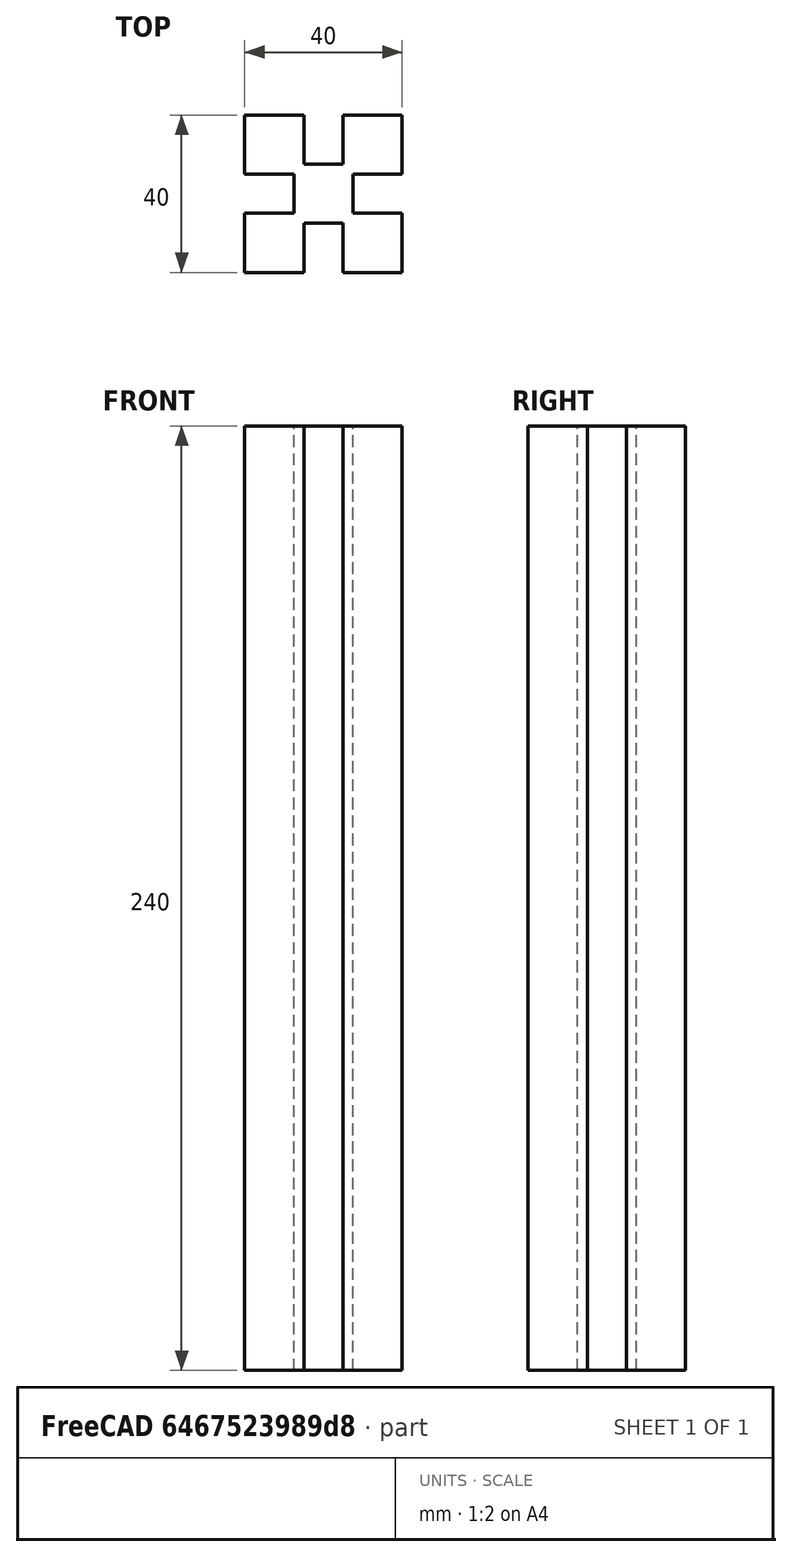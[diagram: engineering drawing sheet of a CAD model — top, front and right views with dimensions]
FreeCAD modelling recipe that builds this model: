
FCSTD DOCUMENT  (FreeCAD 0.18R14555 (Git shallow))
Label: t-slot-profile-240
License: All rights reserved
LicenseURL: http://en.wikipedia.org/wiki/All_rights_reserved
objects: Sketcher::SketchObject×1, PartDesign::Pad×1, PartDesign::Body×1
note: 4 computed .brp shape members not serialized (recipe doc carries the construction recipe); baked Part::Feature solids carry a one-line shape summary decoded from their .brp

FEATURE [Sketcher::SketchObject] Sketch
  MapMode = 5
  Support = -> [XY_Plane]
  sketch-geometry (30):
    g0: LineSegment StartX=-20 StartY=-20 StartZ=0 EndX=-20 EndY=-5 EndZ=0
    g1: LineSegment StartX=-20 StartY=-5 StartZ=0 EndX=-7.5 EndY=-5 EndZ=0
    g2: LineSegment StartX=-7.5 StartY=-5 StartZ=0 EndX=-7.5 EndY=5 EndZ=0
    g3: LineSegment StartX=-7.5 StartY=5 StartZ=0 EndX=-20 EndY=5 EndZ=0
    g4: LineSegment StartX=-20 StartY=5 StartZ=0 EndX=-20 EndY=20 EndZ=0
    g5: LineSegment StartX=-20 StartY=20 StartZ=0 EndX=-5 EndY=20 EndZ=0
    g6: LineSegment StartX=-5 StartY=20 StartZ=0 EndX=-5 EndY=7.5 EndZ=0
    g7: LineSegment StartX=-5 StartY=7.5 StartZ=0 EndX=5 EndY=7.5 EndZ=0
    g8: LineSegment StartX=5 StartY=7.5 StartZ=0 EndX=5 EndY=20 EndZ=0
    g9: LineSegment StartX=5 StartY=20 StartZ=0 EndX=20 EndY=20 EndZ=0
    g10: LineSegment StartX=20 StartY=20 StartZ=0 EndX=20 EndY=5 EndZ=0
    g11: LineSegment StartX=20 StartY=5 StartZ=0 EndX=7.5 EndY=5 EndZ=0
    g12: LineSegment StartX=7.5 StartY=5 StartZ=0 EndX=7.5 EndY=-5 EndZ=0
    g13: LineSegment StartX=7.5 StartY=-5 StartZ=0 EndX=20 EndY=-5 EndZ=0
    g14: LineSegment StartX=20 StartY=-5 StartZ=0 EndX=20 EndY=-20 EndZ=0
    g15: LineSegment StartX=20 StartY=-20 StartZ=0 EndX=5 EndY=-20 EndZ=0
    g16: LineSegment StartX=5 StartY=-20 StartZ=0 EndX=5 EndY=-7.5 EndZ=0
    g17: LineSegment StartX=5 StartY=-7.5 StartZ=0 EndX=-5 EndY=-7.5 EndZ=0
    g18: LineSegment StartX=-5 StartY=-7.5 StartZ=0 EndX=-5 EndY=-20 EndZ=0
    g19: LineSegment StartX=-5 StartY=-20 StartZ=0 EndX=-20 EndY=-20 EndZ=0
    g20: LineSegment [constr] StartX=-5 StartY=-7.5 StartZ=0 EndX=-5 EndY=7.5 EndZ=0
    g21: LineSegment [constr] StartX=5 StartY=7.5 StartZ=0 EndX=5 EndY=-7.5 EndZ=0
    g22: LineSegment [constr] StartX=-7.5 StartY=5 StartZ=0 EndX=7.5 EndY=5 EndZ=0
    g23: LineSegment [constr] StartX=7.5 StartY=-5 StartZ=0 EndX=-7.5 EndY=-5 EndZ=0
    g24: LineSegment [constr] StartX=-20 StartY=-5 StartZ=0 EndX=-20 EndY=5 EndZ=0
    g25: LineSegment [constr] StartX=-5 StartY=20 StartZ=0 EndX=5 EndY=20 EndZ=0
    g26: LineSegment [constr] StartX=20 StartY=5 StartZ=0 EndX=20 EndY=-5 EndZ=0
    g27: LineSegment [constr] StartX=-5 StartY=-20 StartZ=0 EndX=5 EndY=-20 EndZ=0
    g28: LineSegment [constr] StartX=20 StartY=-20 StartZ=0 EndX=-20 EndY=20 EndZ=0
    g29: LineSegment [constr] StartX=-20 StartY=-20 StartZ=0 EndX=20 EndY=20 EndZ=0
  constraints (80):
    c: Vertical(g0)
    c: Coincident(g0,g1)
    c: Horizontal(g1)
    c: Coincident(g1,g2)
    c: Vertical(g2)
    c: Coincident(g2,g3)
    c: Horizontal(g3)
    c: Coincident(g3,g4)
    c: Vertical(g4)
    c: Coincident(g4,g5)
    c: Horizontal(g5)
    c: Coincident(g5,g6)
    c: Vertical(g6)
    c: Coincident(g6,g7)
    c: Horizontal(g7)
    c: Coincident(g7,g8)
    c: Vertical(g8)
    c: Coincident(g8,g9)
    c: Horizontal(g9)
    c: Coincident(g9,g10)
    c: Vertical(g10)
    c: Coincident(g10,g11)
    c: Coincident(g11,g12)
    c: Coincident(g12,g13)
    c: Horizontal(g13)
    c: Coincident(g13,g14)
    c: Vertical(g14)
    c: Coincident(g14,g15)
    c: Horizontal(g15)
    c: Coincident(g15,g16)
    c: Vertical(g16)
    c: Coincident(g16,g17)
    c: Horizontal(g17)
    c: Coincident(g17,g18)
    c: Vertical(g18)
    c: Coincident(g18,g19)
    c: Coincident(g19,g0)
    c: Horizontal(g19)
    c: Horizontal(g11)
    c: Vertical(g12)
    c: Coincident(g20,g17)
    c: Coincident(g20,g6)
    c: Coincident(g21,g7)
    c: Coincident(g21,g16)
    c: Vertical(g21)
    c: Vertical(g20)
    c: Coincident(g22,g2)
    c: Coincident(g22,g11)
    c: Coincident(g23,g12)
    c: Coincident(g23,g1)
    c: Horizontal(g23)
    c: Horizontal(g22)
    c: Coincident(g24,g0)
    c: Coincident(g24,g3)
    c: Vertical(g24)
    c: Coincident(g25,g5)
    c: Coincident(g25,g8)
    c: Horizontal(g25)
    c: Coincident(g26,g10)
    c: Coincident(g26,g13)
    c: Vertical(g26)
    c: Coincident(g27,g18)
    c: Coincident(g27,g15)
    c: Horizontal(g27)
    c: Coincident(g28,g14)
    c: Coincident(g29,g0)
    c: Coincident(g29,g9)
    c: Coincident(g28,g4)
    c: Equal(g0,g19)
    c: Equal(g4,g5)
    c: Equal(g9,g10)
    c: Equal(g2,g7)
    c: Equal(g3,g6)
    c: Equal(g11,g3)
    c: Equal(g1,g18)
    c: DistanceY(g0,g4) = 40
    c: DistanceY(g2,g2) = 10
    c: DistanceY(g18,g18) = 12.5
    c: PointOnObject(g-1,g29)
    c: PointOnObject(g-1,g28)
FEATURE [PartDesign::Pad] Pad
  Length = 240
  Length2 = 100
  Profile = -> Sketch
  Type = 0
FEATURE [PartDesign::Body] Body
  Group = -> [Sketch,Pad]
  Origin = -> Origin
  Tip = -> Pad
